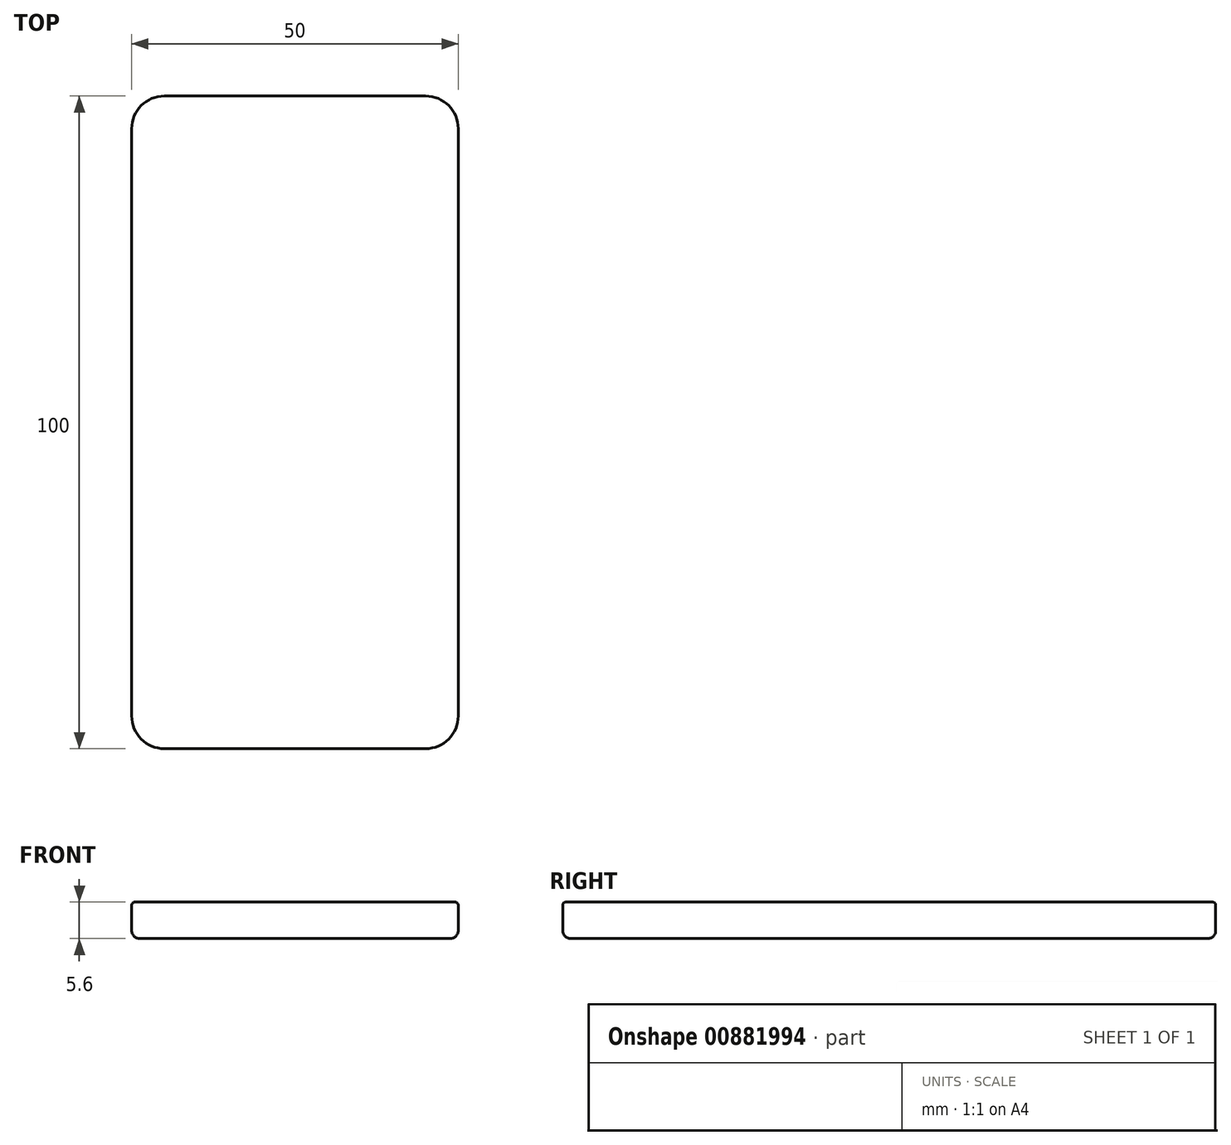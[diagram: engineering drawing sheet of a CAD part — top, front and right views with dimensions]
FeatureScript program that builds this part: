
annotation { "Feature Type Name" : "Feature", "Feature Type Description" : "" }
export const myFeature = defineFeature(function(context is Context, id is Id, definition is map)
    precondition{}
    {
        {
            var Q0;
            Q0=qCreatedBy(makeId("Top.planeOp"),FACE);
            var sketch = newSketch(context, id + "F0", { "sketchPlane" : qUnion([Q0])});
            skLineSegment(sketch, "E0.bottom", {"start": v(-20, 50) * mm, "end": v(20, 50) * mm});
            skLineSegment(sketch, "E0.top", {"start": v(-20, -50) * mm, "end": v(20, -50) * mm});
            skLineSegment(sketch, "E0.left", {"start": v(-25, 45) * mm, "end": v(-25, -45) * mm});
            skLineSegment(sketch, "E0.right", {"start": v(25, 45) * mm, "end": v(25, -45) * mm});
            skPoint(sketch, "E0.middle", {"position": v(0, 0) * mm});
            skPoint(sketch, "E1.visualSharp", {"position": v(25, 50) * mm});
            skArc(sketch, "E1.filletArc", {"start": v(25, 45) * mm, "mid": v(23.54, 48.54) * mm, "end": v(20, 50) * mm});
            skPoint(sketch, "E2.visualSharp", {"position": v(25, -50) * mm});
            skArc(sketch, "E2.filletArc", {"start": v(20, -50) * mm, "mid": v(23.54, -48.54) * mm, "end": v(25, -45) * mm});
            skPoint(sketch, "E3.visualSharp", {"position": v(-25, -50) * mm});
            skArc(sketch, "E3.filletArc", {"start": v(-25, -45) * mm, "mid": v(-23.54, -48.54) * mm, "end": v(-20, -50) * mm});
            skPoint(sketch, "E4.visualSharp", {"position": v(-25, 50) * mm});
            skArc(sketch, "E4.filletArc", {"start": v(-20, 50) * mm, "mid": v(-23.54, 48.54) * mm, "end": v(-25, 45) * mm});
            skSolve(sketch);
        }
        {
            var Q0;
            Q0=makeQuery(id+"F0.imprint","IMPRINT",FACE,{"disambiguationData":[TD([[makeQuery(id+"F0.imprint","IMPRINT",EDGE,{"derivedFrom":sQuery(id+"F0.wireOp",EDGE,"E0.bottom")}),-1.0]])]});
            extrude(context, id + "F1", {"entities" : qUnion([Q0]), "depth" : 5.6 * mm, "offsetDistance" : 25 * mm});
        }
        {
            var Q0;
            Q0=makeQuery(id+"F1.opExtrude","CAP_EDGE",EDGE,{"disambiguationData":[OSD([sQuery(id+"F0.wireOp",EDGE,"E0.left")])],"isStart":true});
            fillet(context, id + "F2", {"entities" : qUnion([Q0]), "radius" : 1.2 * mm, "tangentPropagation" : true, "allowEdgeOverflow" : false});
        }
        {
            var Q0;
            Q0=makeQuery(id+"F1.opExtrude","CAP_EDGE",EDGE,{"disambiguationData":[OSD([sQuery(id+"F0.wireOp",EDGE,"E0.right")])],"isStart":false});
            fillet(context, id + "F3", {"entities" : qUnion([Q0]), "radius" : 0.48 * mm, "tangentPropagation" : true, "allowEdgeOverflow" : false});
        }
    });
